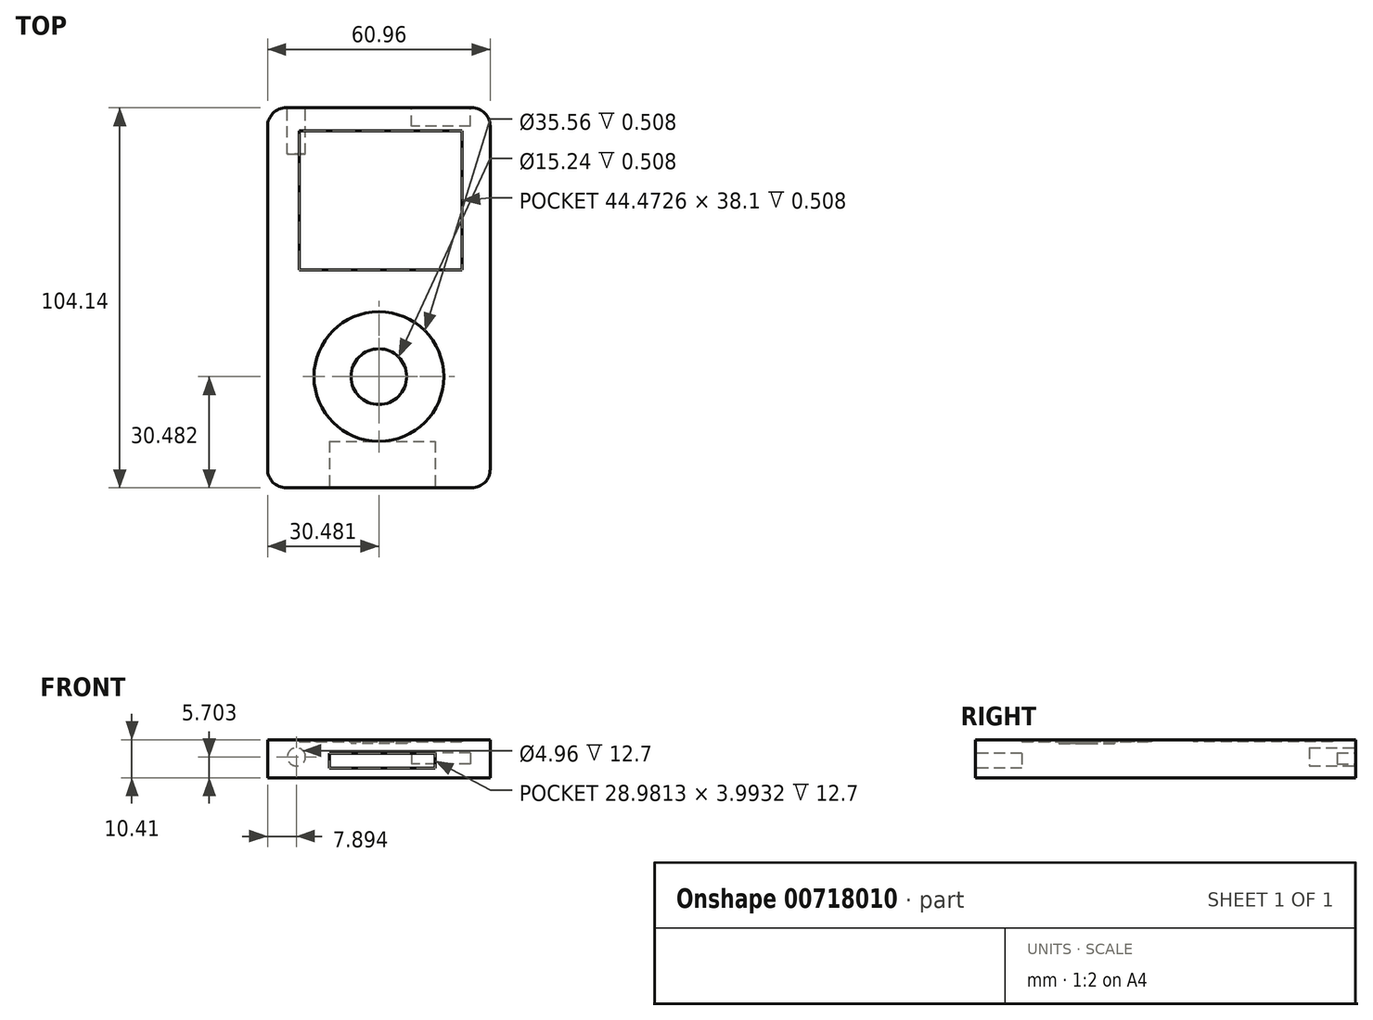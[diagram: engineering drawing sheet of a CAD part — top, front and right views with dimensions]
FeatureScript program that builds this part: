
annotation { "Feature Type Name" : "Feature", "Feature Type Description" : "" }
export const myFeature = defineFeature(function(context is Context, id is Id, definition is map)
    precondition{}
    {
        {
            var Q0;
            Q0=qCreatedBy(makeId("Top.planeOp"),FACE);
            var sketch = newSketch(context, id + "F0", { "sketchPlane" : qUnion([Q0])});
            skLineSegment(sketch, "E0.bottom", {"start": v(-33.1, 46.96) * mm, "end": v(27.85, 46.96) * mm});
            skLineSegment(sketch, "E0.top", {"start": v(-33.1, -57.18) * mm, "end": v(27.85, -57.18) * mm});
            skLineSegment(sketch, "E0.left", {"start": v(-33.1, 46.96) * mm, "end": v(-33.1, -57.18) * mm});
            skLineSegment(sketch, "E0.right", {"start": v(27.85, 46.96) * mm, "end": v(27.85, -57.18) * mm});
            skLineSegment(sketch, "E1.bottom", {"start": v(-24.37, 40.61) * mm, "end": v(20.1, 40.61) * mm});
            skLineSegment(sketch, "E1.top", {"start": v(-24.37, 2.51) * mm, "end": v(20.1, 2.51) * mm});
            skLineSegment(sketch, "E1.left", {"start": v(-24.37, 40.61) * mm, "end": v(-24.37, 2.51) * mm});
            skLineSegment(sketch, "E1.right", {"start": v(20.1, 40.61) * mm, "end": v(20.1, 2.51) * mm});
            skCircle(sketch, "E2", {"center": v(-2.63, -26.7) * mm, "radius": 7.62 * mm});
            skCircle(sketch, "E3", {"center": v(-2.63, -26.7) * mm, "radius": 17.78 * mm});
            skSolve(sketch);
        }
        {
            var Q0;
            Q0 = qSketchRegion(id + "F0", true);
            extrude(context, id + "F1", {"entities" : qUnion([Q0]), "depth" : 10.4 * mm, "offsetDistance" : 25.4 * mm});
        }
        {
            var Q0;
            Q0=makeQuery(id+"F0.imprint","IMPRINT",FACE,{"disambiguationData":[TD([[makeQuery(id+"F0.imprint","IMPRINT",EDGE,{"derivedFrom":sQuery(id+"F0.wireOp",EDGE,"E1.bottom")}),-1.0]])]});
            var Q1;
            Q1=makeQuery(id+"F0.imprint","IMPRINT",FACE,{"disambiguationData":[TD([[makeQuery(id+"F0.imprint","IMPRINT",EDGE,{"derivedFrom":sQuery(id+"F0.wireOp",EDGE,"E2")}),-1.0]])]});
            extrude(context, id + "F2", {"entities" : qUnion([Q0, Q1]), "operationType" : NewBodyOperationType.ADD, "depth" : 9.9 * mm, "offsetDistance" : 25.4 * mm});
        }
        {
            var Q0;
            Q0=makeQuery(id+"F0.imprint","IMPRINT",FACE,{"disambiguationData":[TD([[makeQuery(id+"F0.imprint","IMPRINT",EDGE,{"derivedFrom":sQuery(id+"F0.wireOp",EDGE,"E2")}),1.0]])]});
            extrude(context, id + "F3", {"entities" : qUnion([Q0]), "operationType" : NewBodyOperationType.ADD, "depth" : 9.4 * mm, "offsetDistance" : 25.4 * mm});
        }
        {
            var Q0;
            Q0=makeQuery(id+"F1.opExtrude","SWEPT_FACE",FACE,{"disambiguationData":[OSD([sQuery(id+"F0.wireOp",EDGE,"E0.bottom")])]});
            var sketch = newSketch(context, id + "F4", { "sketchPlane" : qUnion([Q0])});
            skLineSegment(sketch, "E4.bottom", {"start": v(-22.36, 6.76) * mm, "end": v(-6.34, 6.76) * mm});
            skLineSegment(sketch, "E4.top", {"start": v(-22.36, 3.8) * mm, "end": v(-6.34, 3.8) * mm});
            skLineSegment(sketch, "E4.left", {"start": v(-22.36, 6.76) * mm, "end": v(-22.36, 3.8) * mm});
            skLineSegment(sketch, "E4.right", {"start": v(-6.34, 6.76) * mm, "end": v(-6.34, 3.8) * mm});
            skCircle(sketch, "E5", {"center": v(25.22, 5.7) * mm, "radius": 2.48 * mm});
            skSolve(sketch);
        }
        {
            var Q0;
            Q0=makeQuery(id+"F4.imprint","IMPRINT",FACE,{"disambiguationData":[TD([[makeQuery(id+"F4.imprint","IMPRINT",EDGE,{"derivedFrom":sQuery(id+"F4.wireOp",EDGE,"E4.bottom")}),-1.0]])]});
            extrude(context, id + "F5", {"entities" : qUnion([Q0]), "operationType" : NewBodyOperationType.REMOVE, "oppositeDirection" : true, "depth" : 5.08 * mm, "offsetDistance" : 25.4 * mm});
        }
        {
            var Q0;
            Q0=makeQuery(id+"F4.imprint","IMPRINT",FACE,{"disambiguationData":[TD([[makeQuery(id+"F4.imprint","IMPRINT",EDGE,{"derivedFrom":sQuery(id+"F4.wireOp",EDGE,"E5")}),1.0]])]});
            extrude(context, id + "F6", {"entities" : qUnion([Q0]), "operationType" : NewBodyOperationType.REMOVE, "oppositeDirection" : true, "depth" : 12.7 * mm, "offsetDistance" : 25.4 * mm});
        }
        {
            var Q0;
            Q0=makeQuery(id+"F1.opExtrude","SWEPT_EDGE",EDGE,{"disambiguationData":[OSD([sQuery(id+"F0.wireOp",EDGE,"E0.bottom"),sQuery(id+"F0.wireOp",EDGE,"E0.left")])]});
            var Q1;
            Q1=makeQuery(id+"F1.opExtrude","SWEPT_EDGE",EDGE,{"disambiguationData":[OSD([sQuery(id+"F0.wireOp",EDGE,"E0.bottom"),sQuery(id+"F0.wireOp",EDGE,"E0.right")])]});
            var Q2;
            Q2=makeQuery(id+"F1.opExtrude","SWEPT_EDGE",EDGE,{"disambiguationData":[OSD([sQuery(id+"F0.wireOp",EDGE,"E0.top"),sQuery(id+"F0.wireOp",EDGE,"E0.right")])]});
            var Q3;
            Q3=makeQuery(id+"F1.opExtrude","SWEPT_EDGE",EDGE,{"disambiguationData":[OSD([sQuery(id+"F0.wireOp",EDGE,"E0.top"),sQuery(id+"F0.wireOp",EDGE,"E0.left")])]});
            fillet(context, id + "F7", {"entities" : qUnion([Q0, Q1, Q2, Q3]), "radius" : 5.08 * mm, "tangentPropagation" : true, "allowEdgeOverflow" : false});
        }
        {
            var Q0;
            Q0=makeQuery(id+"F1.opExtrude","SWEPT_FACE",FACE,{"disambiguationData":[OSD([sQuery(id+"F0.wireOp",EDGE,"E0.top")])]});
            var sketch = newSketch(context, id + "F8", { "sketchPlane" : qUnion([Q0])});
            skLineSegment(sketch, "E6.bottom", {"start": v(-16.24, 6.66) * mm, "end": v(12.74, 6.66) * mm});
            skLineSegment(sketch, "E6.top", {"start": v(-16.24, 2.67) * mm, "end": v(12.74, 2.67) * mm});
            skLineSegment(sketch, "E6.left", {"start": v(-16.24, 6.66) * mm, "end": v(-16.24, 2.67) * mm});
            skLineSegment(sketch, "E6.right", {"start": v(12.74, 6.66) * mm, "end": v(12.74, 2.67) * mm});
            skSolve(sketch);
        }
        {
            var Q0;
            Q0=makeQuery(id+"F8.imprint","IMPRINT",FACE,{"disambiguationData":[TD([[makeQuery(id+"F8.imprint","IMPRINT",EDGE,{"derivedFrom":sQuery(id+"F8.wireOp",EDGE,"E6.bottom")}),-1.0]])]});
            extrude(context, id + "F9", {"entities" : qUnion([Q0]), "operationType" : NewBodyOperationType.REMOVE, "oppositeDirection" : true, "depth" : 12.7 * mm, "offsetDistance" : 25.4 * mm});
        }
    });
